# Revit family: Bath-Freestanding-KOHLER-ALEUTIAN-K-99023T_1
name_source: partatom
category: Plumbing Fixtures
revit_build: Autodesk Revit 2017 (Build: 20160225_1515(x64)
units: mm (PartAtom-declared; Revit-internal decimal feet)

## family parameters
Cut with Voids When Loaded = No
Host = Face
OmniClass Number = 23.31.15.00
OmniClass Title = Bathtubs
Part Type = Normal
Room Calculation Point = No
Round Connector Dimension = Use Diameter
Shared = No

## types (1)
- 0-White
    ADA Compliant = No
    Assembly Code = D2010500
    CW Connection = No
    Cold Water Inlet = Cold Water Inlet
    Date Modified = 01/16/2021
    Default Elevation = 0"
    Description = INTEGRATED ALEUTIAN 1.7M BATH LEFT-HAND CORNER
    Drain Included = No
    Finish = KOHLER-Acrylic-0-White
    HW Connection = No
    Height = 25 5/8"
    Hot Water Inlet = Hot Water Inlet
    Length = 31 1/2"
    Manufacturer = KOHLER Co.
    Master Format 2014 = 22 41 19
    Master Format 2014 Name = Residential Bathtubs
    Material = Acrylic
    Model = K-99023T-0
    Product Documentation Link = https://files.kohler.com.cn
    Product Name = ALEUTIAN
    Product Page URL = https://www.kohler.com.cn
    Type = 1
    URL = http://www.kohler.com.cn
    Vent Connection = No
    Waste Connection = Yes
    Waste Water Outlet = Waste Water Outlet
    WaterSense Certified = No
    Width = 67 1/16"

## geometry (parser evidence)
native form markers: Sweep x5
no freeform markers — native parametric forms only
